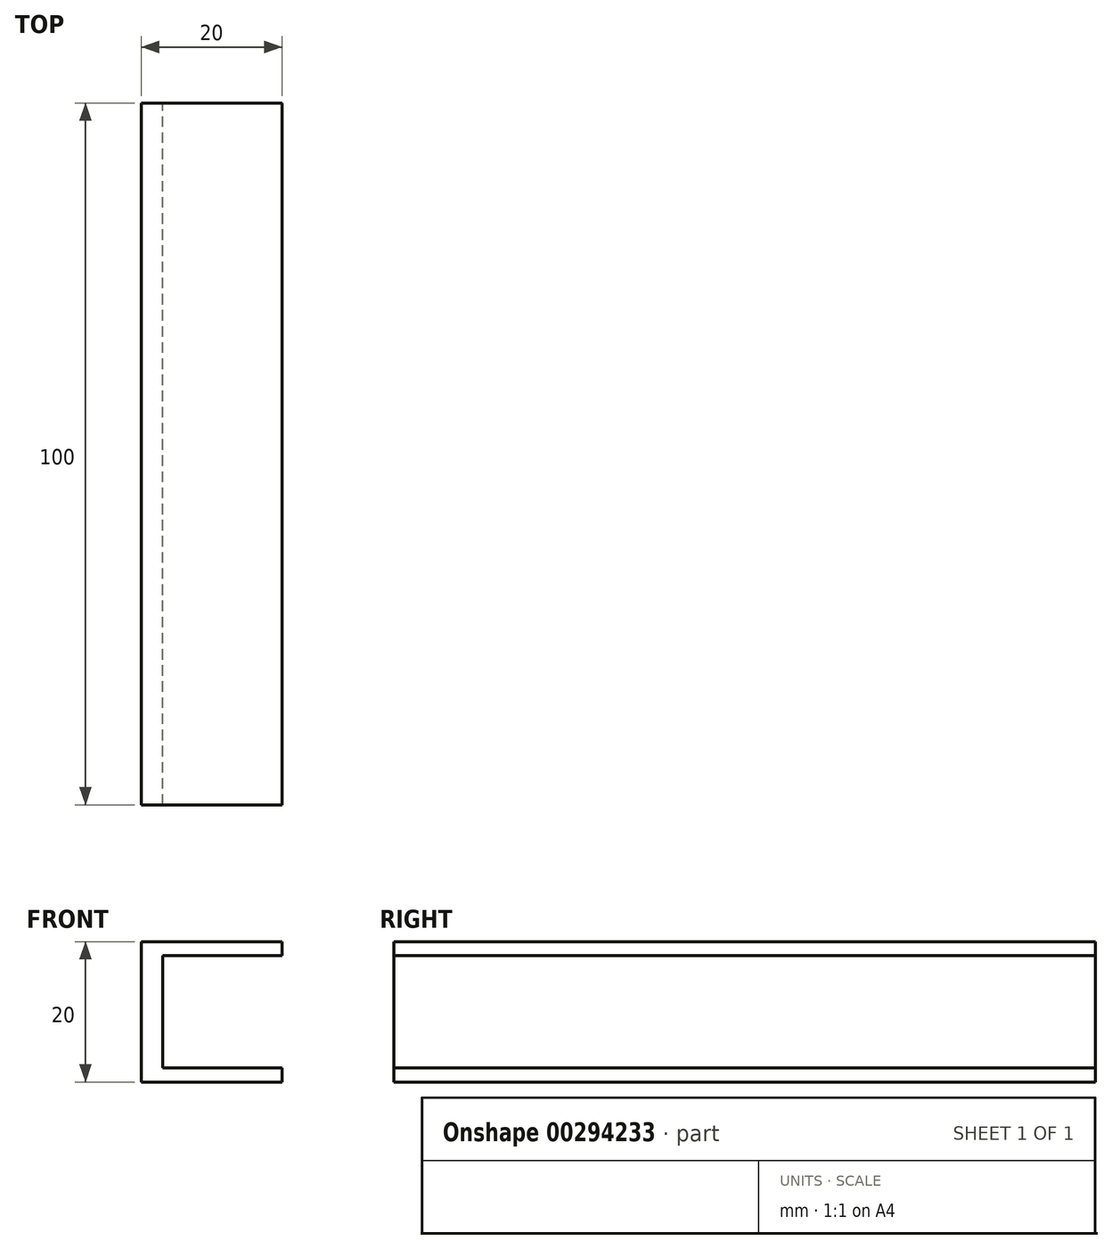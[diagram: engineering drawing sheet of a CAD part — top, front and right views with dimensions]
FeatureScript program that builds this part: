
annotation { "Feature Type Name" : "Feature", "Feature Type Description" : "" }
export const myFeature = defineFeature(function(context is Context, id is Id, definition is map)
    precondition{}
    {
        {
            var Q0;
            Q0=qCreatedBy(makeId("Front.planeOp"),FACE);
            var sketch = newSketch(context, id + "F0", { "sketchPlane" : qUnion([Q0])});
            skLineSegment(sketch, "E0.bottom", {"start": v(0, 0) * mm, "end": v(-20, 0) * mm});
            skLineSegment(sketch, "E0.top", {"start": v(0, 20) * mm, "end": v(-20, 20) * mm});
            skLineSegment(sketch, "E0.left", {"start": v(0, 0) * mm, "end": v(0, 2) * mm});
            skLineSegment(sketch, "E0.right", {"start": v(-20, 0) * mm, "end": v(-20, 20) * mm});
            skLineSegment(sketch, "E1", {"start": v(0, 18) * mm, "end": v(-17, 18) * mm});
            skLineSegment(sketch, "E2", {"start": v(-17, 18) * mm, "end": v(-17, 2) * mm});
            skLineSegment(sketch, "E3", {"start": v(-17, 2) * mm, "end": v(0, 2) * mm});
            skLineSegment(sketch, "E4.trimOffspring", {"start": v(0, 18) * mm, "end": v(0, 20) * mm});
            skSolve(sketch);
        }
        {
            var Q0;
            Q0 = qSketchRegion(id + "F0", true);
            extrude(context, id + "F1", {"entities" : qUnion([Q0]), "depth" : 100 * mm});
        }
    });
